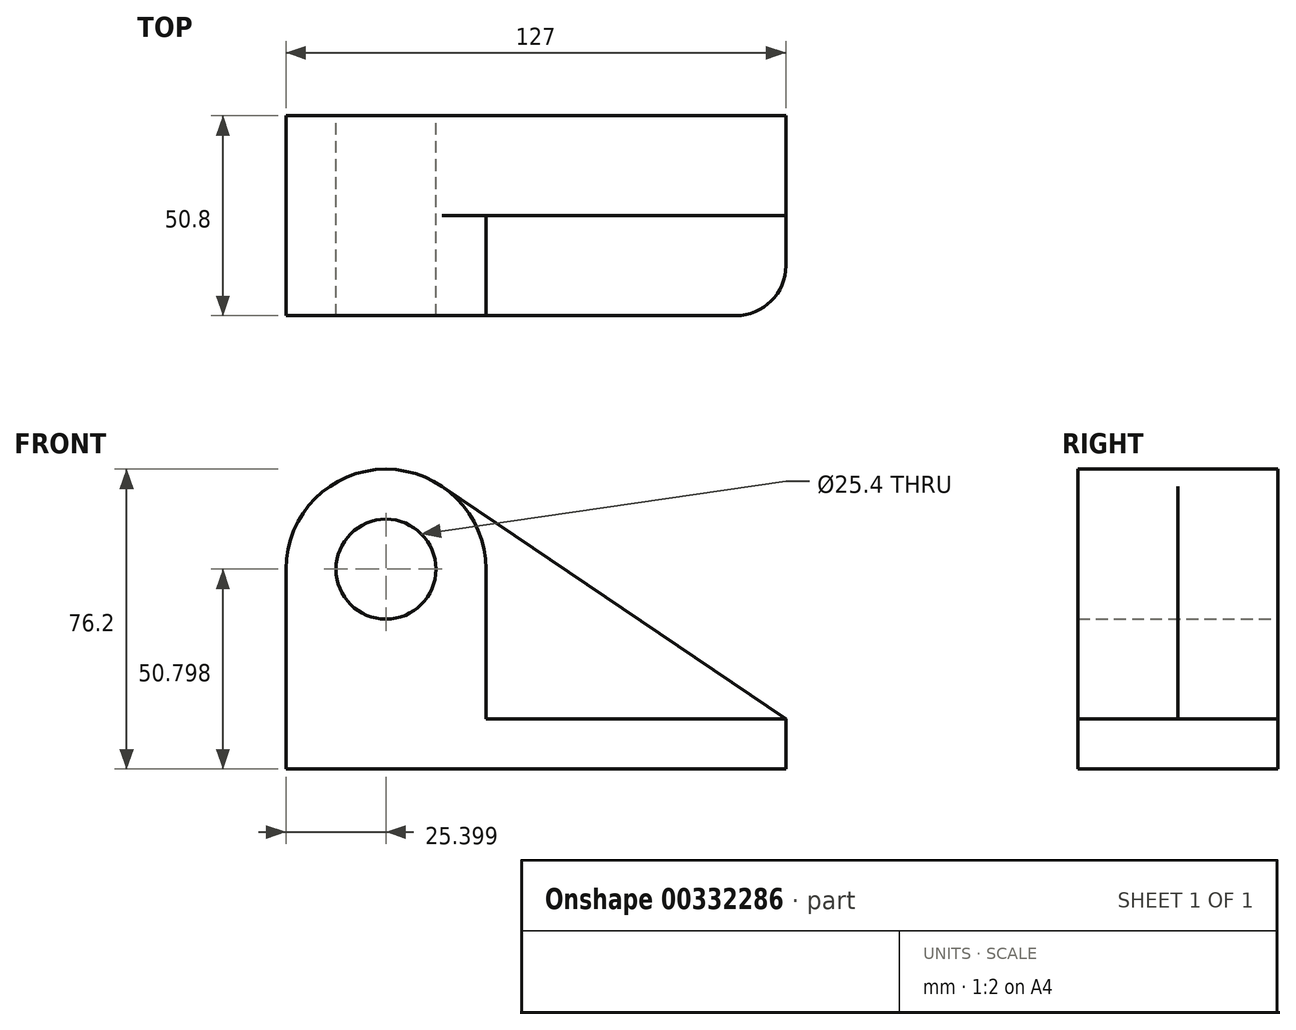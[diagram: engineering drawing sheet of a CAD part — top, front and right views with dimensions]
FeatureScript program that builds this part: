
annotation { "Feature Type Name" : "Feature", "Feature Type Description" : "" }
export const myFeature = defineFeature(function(context is Context, id is Id, definition is map)
    precondition{}
    {
        {
            var Q0;
            Q0=qCreatedBy(makeId("Front.planeOp"),FACE);
            var sketch = newSketch(context, id + "F0", { "sketchPlane" : qUnion([Q0])});
            skCircle(sketch, "E0", {"center": v(-22.9, 11) * mm, "radius": 12.7 * mm});
            skCircle(sketch, "E1", {"center": v(-22.9, 11) * mm, "radius": 25.4 * mm});
            skLineSegment(sketch, "E2", {"start": v(-48.3, 11) * mm, "end": v(-48.3, -39.8) * mm});
            skLineSegment(sketch, "E3", {"start": v(-48.3, -39.8) * mm, "end": v(78.7, -39.8) * mm});
            skLineSegment(sketch, "E4", {"start": v(78.7, -27.1) * mm, "end": v(78.7, -39.8) * mm});
            skLineSegment(sketch, "E5", {"start": v(78.7, -27.1) * mm, "end": v(-8.65, 32.04) * mm});
            skSolve(sketch);
        }
        {
            var Q0;
            Q0 = qSketchRegion(id + "F0", true);
            extrude(context, id + "F1", {"entities" : qUnion([Q0]), "depth" : 25.4 * mm});
        }
        {
            var Q0;
            Q0=makeQuery(id+"F1.opExtrude","CAP_FACE",FACE,{"disambiguationData":[OSD([sQuery(id+"F0.wireOp",EDGE,"E0"),sQuery(id+"F0.wireOp",EDGE,"E1"),sQuery(id+"F0.wireOp",EDGE,"E2"),sQuery(id+"F0.wireOp",EDGE,"E3"),sQuery(id+"F0.wireOp",EDGE,"E4"),sQuery(id+"F0.wireOp",EDGE,"E5")])],"isStart":false});
            var sketch = newSketch(context, id + "F2", { "sketchPlane" : qUnion([Q0])});
            skCircle(sketch, "E6", {"center": v(-22.9, 11) * mm, "radius": 12.7 * mm});
            skArc(sketch, "E7", {"start": v(2.5, 11) * mm, "mid": v(-22.9, 36.4) * mm, "end": v(-48.3, 11) * mm});
            skLineSegment(sketch, "E8.bottom", {"start": v(78.7, -27.1) * mm, "end": v(2.5, -27.1) * mm});
            skLineSegment(sketch, "E8.top", {"start": v(78.7, -39.8) * mm, "end": v(-48.3, -39.8) * mm});
            skLineSegment(sketch, "E8.left", {"start": v(78.7, -27.1) * mm, "end": v(78.7, -39.8) * mm});
            skLineSegment(sketch, "E8.right", {"start": v(-48.3, -27.1) * mm, "end": v(-48.3, -39.8) * mm});
            skLineSegment(sketch, "E9", {"start": v(-48.3, 11) * mm, "end": v(-48.3, -27.1) * mm});
            skLineSegment(sketch, "E10", {"start": v(2.5, 11) * mm, "end": v(2.5, -27.1) * mm});
            skSolve(sketch);
        }
        {
            var Q0;
            Q0 = qSketchRegion(id + "F2", true);
            extrude(context, id + "F3", {"entities" : qUnion([Q0]), "operationType" : NewBodyOperationType.ADD, "depth" : 25.4 * mm});
        }
        {
            var Q0;
            Q0=makeQuery(id+"F3.opExtrude","CAP_EDGE",EDGE,{"disambiguationData":[OSD([sQuery(id+"F2.wireOp",EDGE,"E8.left")])],"isStart":false});
            fillet(context, id + "F4", {"entities" : qUnion([Q0]), "radius" : 12.7 * mm, "tangentPropagation" : true, "allowEdgeOverflow" : false});
        }
    });
